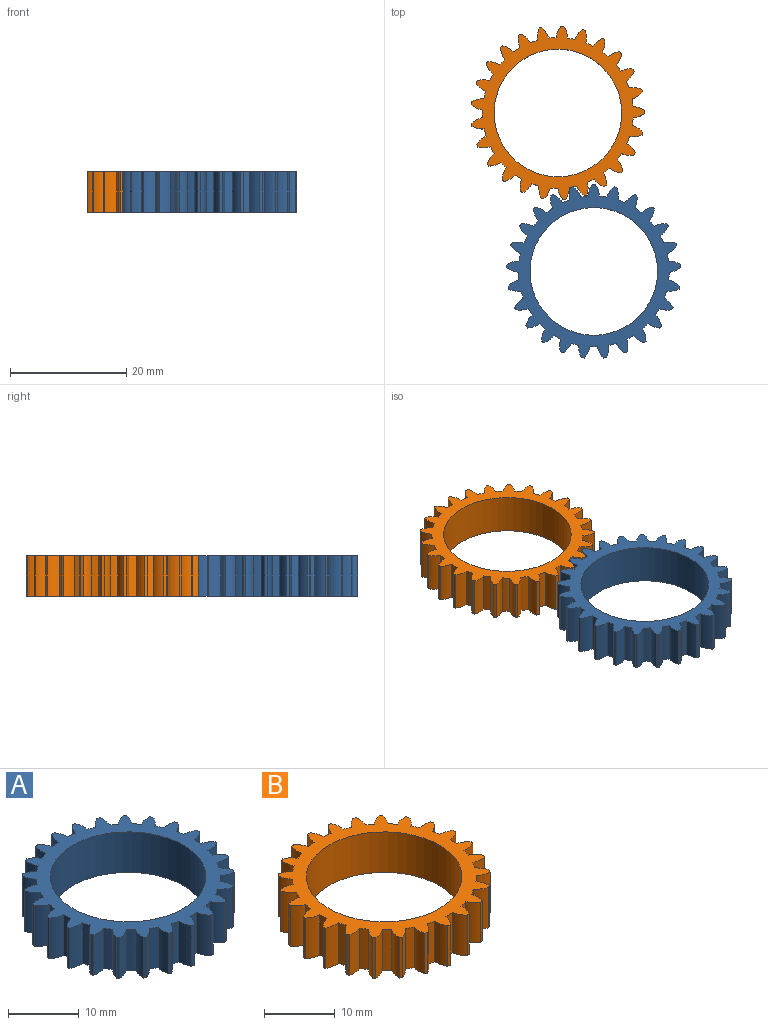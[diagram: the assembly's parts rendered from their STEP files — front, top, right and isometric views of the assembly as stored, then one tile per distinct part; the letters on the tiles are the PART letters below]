
ASSEMBLY  parts=2 mates=1
PART A: 103 faces, bbox 30x29.9x7 mm
  f0: cylinder r=4mm len=7mm, axis (0,0,-1), area 15.4mm2, adj f1,f3,f4,f32
  f1: cylinder r=15mm len=7mm, axis (0,0,-1), area 3.3mm2, adj f0,f2,f3,f4
  f2: cylinder r=4mm len=7mm, axis (0,0,-1), area 15.4mm2, adj f1,f3,f4,f5
  f3: plane 29.97x29.91mm, normal (0,0,1), area 222.8mm2, adj f0,f1,f2,f5,f6,f7,f8,f9
  f4: plane 29.97x29.91mm, normal (0,0,-1), area 222.8mm2, adj f0,f1,f2,f5,f6,f7,f8,f9
  f5: cylinder r=13mm len=7mm, axis (0,0,-1), area 9mm2, adj f2,f3,f4,f6
  f6: cylinder r=4mm len=7mm, axis (0,0,-1), area 15.4mm2, adj f3,f4,f5,f7
  f7: cylinder r=15mm len=7mm, axis (0,0,-1), area 3.3mm2, adj f3,f4,f6,f8
  f8: cylinder r=4mm len=7mm, axis (0,0,-1), area 15.4mm2, adj f3,f4,f7,f9
  f9: cylinder r=13mm len=7mm, axis (0,0,-1), area 9mm2, adj f3,f4,f8,f34
  f10: cylinder r=13mm len=7mm, axis (0,0,-1), area 9mm2, adj f3,f4,f99,f100
  f11: cylinder r=13mm len=7mm, axis (0,0,-1), area 9mm2, adj f3,f4,f96,f97
  f12: cylinder r=13mm len=7mm, axis (0,0,-1), area 9mm2, adj f3,f4,f93,f94
  f13: cylinder r=13mm len=7mm, axis (0,0,-1), area 9mm2, adj f3,f4,f90,f91
  f14: cylinder r=13mm len=7mm, axis (0,0,-1), area 9mm2, adj f3,f4,f87,f88
  f15: cylinder r=13mm len=7mm, axis (0,0,-1), area 9mm2, adj f3,f4,f84,f85
  f16: cylinder r=13mm len=7mm, axis (0,0,-1), area 9mm2, adj f3,f4,f81,f82
  f17: cylinder r=13mm len=7mm, axis (0,0,-1), area 9mm2, adj f3,f4,f78,f79
  f18: cylinder r=13mm len=7mm, axis (0,0,-1), area 9mm2, adj f3,f4,f75,f76
  f19: cylinder r=13mm len=7mm, axis (0,0,-1), area 9mm2, adj f3,f4,f72,f73
  f20: cylinder r=13mm len=7mm, axis (0,0,-1), area 9mm2, adj f3,f4,f69,f70
  f21: cylinder r=13mm len=7mm, axis (0,0,-1), area 9mm2, adj f3,f4,f66,f67
  f22: cylinder r=13mm len=7mm, axis (0,0,-1), area 9mm2, adj f3,f4,f63,f64
  f23: cylinder r=13mm len=7mm, axis (0,0,-1), area 9mm2, adj f3,f4,f60,f61
  f24: cylinder r=13mm len=7mm, axis (0,0,-1), area 9mm2, adj f3,f4,f57,f58
  f25: cylinder r=13mm len=7mm, axis (0,0,-1), area 9mm2, adj f3,f4,f54,f55
  f26: cylinder r=13mm len=7mm, axis (0,0,-1), area 9mm2, adj f3,f4,f51,f52
  f27: cylinder r=13mm len=7mm, axis (0,0,-1), area 9mm2, adj f3,f4,f48,f49
  f28: cylinder r=13mm len=7mm, axis (0,0,-1), area 9mm2, adj f3,f4,f45,f46
  f29: cylinder r=13mm len=7mm, axis (0,0,-1), area 9mm2, adj f3,f4,f42,f43
  f30: cylinder r=13mm len=7mm, axis (0,0,-1), area 9mm2, adj f3,f4,f39,f40
  f31: cylinder r=13mm len=7mm, axis (0,0,-1), area 9mm2, adj f3,f4,f36,f37
  f32: cylinder r=13mm len=7mm, axis (0,0,-1), area 9mm2, adj f0,f3,f4,f102
  f33: cylinder r=11mm len=22mm, axis (0,0,-1), area 483.8mm2, adj f3,f4
  f34: cylinder r=4mm len=7mm, axis (0,0,-1), area 15.4mm2, adj f3,f4,f9,f35
  f35: cylinder r=15mm len=7mm, axis (0,0,-1), area 3.3mm2, adj f3,f4,f34,f36
  f36: cylinder r=4mm len=7mm, axis (0,0,-1), area 15.4mm2, adj f3,f4,f31,f35
  f37: cylinder r=4mm len=7mm, axis (0,0,-1), area 15.4mm2, adj f3,f4,f31,f38
  f38: cylinder r=15mm len=7mm, axis (0,0,-1), area 3.3mm2, adj f3,f4,f37,f39
  f39: cylinder r=4mm len=7mm, axis (0,0,-1), area 15.4mm2, adj f3,f4,f30,f38
  f40: cylinder r=4mm len=7mm, axis (0,0,-1), area 15.4mm2, adj f3,f4,f30,f41
  f41: cylinder r=15mm len=7mm, axis (0,0,-1), area 3.3mm2, adj f3,f4,f40,f42
  f42: cylinder r=4mm len=7mm, axis (0,0,-1), area 15.4mm2, adj f3,f4,f29,f41
  f43: cylinder r=4mm len=7mm, axis (0,0,-1), area 15.4mm2, adj f3,f4,f29,f44
  f44: cylinder r=15mm len=7mm, axis (0,0,-1), area 3.3mm2, adj f3,f4,f43,f45
  f45: cylinder r=4mm len=7mm, axis (0,0,-1), area 15.4mm2, adj f3,f4,f28,f44
  f46: cylinder r=4mm len=7mm, axis (0,0,-1), area 15.4mm2, adj f3,f4,f28,f47
  f47: cylinder r=15mm len=7mm, axis (0,0,-1), area 3.3mm2, adj f3,f4,f46,f48
  f48: cylinder r=4mm len=7mm, axis (0,0,-1), area 15.4mm2, adj f3,f4,f27,f47
  f49: cylinder r=4mm len=7mm, axis (0,0,-1), area 15.4mm2, adj f3,f4,f27,f50
  f50: cylinder r=15mm len=7mm, axis (0,0,-1), area 3.3mm2, adj f3,f4,f49,f51
  f51: cylinder r=4mm len=7mm, axis (0,0,-1), area 15.4mm2, adj f3,f4,f26,f50
  f52: cylinder r=4mm len=7mm, axis (0,0,-1), area 15.4mm2, adj f3,f4,f26,f53
  f53: cylinder r=15mm len=7mm, axis (0,0,-1), area 3.3mm2, adj f3,f4,f52,f54
  f54: cylinder r=4mm len=7mm, axis (0,0,-1), area 15.4mm2, adj f3,f4,f25,f53
  f55: cylinder r=4mm len=7mm, axis (0,0,-1), area 15.4mm2, adj f3,f4,f25,f56
  f56: cylinder r=15mm len=7mm, axis (0,0,-1), area 3.3mm2, adj f3,f4,f55,f57
  f57: cylinder r=4mm len=7mm, axis (0,0,-1), area 15.4mm2, adj f3,f4,f24,f56
  f58: cylinder r=4mm len=7mm, axis (0,0,-1), area 15.4mm2, adj f3,f4,f24,f59
  f59: cylinder r=15mm len=7mm, axis (0,0,-1), area 3.3mm2, adj f3,f4,f58,f60
  f60: cylinder r=4mm len=7mm, axis (0,0,-1), area 15.4mm2, adj f3,f4,f23,f59
  f61: cylinder r=4mm len=7mm, axis (0,0,-1), area 15.4mm2, adj f3,f4,f23,f62
  f62: cylinder r=15mm len=7mm, axis (0,0,-1), area 3.3mm2, adj f3,f4,f61,f63
  f63: cylinder r=4mm len=7mm, axis (0,0,-1), area 15.4mm2, adj f3,f4,f22,f62
  f64: cylinder r=4mm len=7mm, axis (0,0,-1), area 15.4mm2, adj f3,f4,f22,f65
  f65: cylinder r=15mm len=7mm, axis (0,0,-1), area 3.3mm2, adj f3,f4,f64,f66
  f66: cylinder r=4mm len=7mm, axis (0,0,-1), area 15.4mm2, adj f3,f4,f21,f65
  f67: cylinder r=4mm len=7mm, axis (0,0,-1), area 15.4mm2, adj f3,f4,f21,f68
  f68: cylinder r=15mm len=7mm, axis (0,0,-1), area 3.3mm2, adj f3,f4,f67,f69
  f69: cylinder r=4mm len=7mm, axis (0,0,-1), area 15.4mm2, adj f3,f4,f20,f68
  f70: cylinder r=4mm len=7mm, axis (0,0,-1), area 15.4mm2, adj f3,f4,f20,f71
  f71: cylinder r=15mm len=7mm, axis (0,0,-1), area 3.3mm2, adj f3,f4,f70,f72
  f72: cylinder r=4mm len=7mm, axis (0,0,-1), area 15.4mm2, adj f3,f4,f19,f71
  f73: cylinder r=4mm len=7mm, axis (0,0,-1), area 15.4mm2, adj f3,f4,f19,f74
  f74: cylinder r=15mm len=7mm, axis (0,0,-1), area 3.3mm2, adj f3,f4,f73,f75
  f75: cylinder r=4mm len=7mm, axis (0,0,-1), area 15.4mm2, adj f3,f4,f18,f74
  f76: cylinder r=4mm len=7mm, axis (0,0,-1), area 15.4mm2, adj f3,f4,f18,f77
  f77: cylinder r=15mm len=7mm, axis (0,0,-1), area 3.3mm2, adj f3,f4,f76,f78
  f78: cylinder r=4mm len=7mm, axis (0,0,-1), area 15.4mm2, adj f3,f4,f17,f77
  f79: cylinder r=4mm len=7mm, axis (0,0,-1), area 15.4mm2, adj f3,f4,f17,f80
  f80: cylinder r=15mm len=7mm, axis (0,0,-1), area 3.3mm2, adj f3,f4,f79,f81
  f81: cylinder r=4mm len=7mm, axis (0,0,-1), area 15.4mm2, adj f3,f4,f16,f80
  f82: cylinder r=4mm len=7mm, axis (0,0,-1), area 15.4mm2, adj f3,f4,f16,f83
  f83: cylinder r=15mm len=7mm, axis (0,0,-1), area 3.3mm2, adj f3,f4,f82,f84
  f84: cylinder r=4mm len=7mm, axis (0,0,-1), area 15.4mm2, adj f3,f4,f15,f83
  f85: cylinder r=4mm len=7mm, axis (0,0,-1), area 15.4mm2, adj f3,f4,f15,f86
  f86: cylinder r=15mm len=7mm, axis (0,0,-1), area 3.3mm2, adj f3,f4,f85,f87
  f87: cylinder r=4mm len=7mm, axis (0,0,-1), area 15.4mm2, adj f3,f4,f14,f86
  f88: cylinder r=4mm len=7mm, axis (0,0,-1), area 15.4mm2, adj f3,f4,f14,f89
  f89: cylinder r=15mm len=7mm, axis (0,0,-1), area 3.3mm2, adj f3,f4,f88,f90
  f90: cylinder r=4mm len=7mm, axis (0,0,-1), area 15.4mm2, adj f3,f4,f13,f89
  f91: cylinder r=4mm len=7mm, axis (0,0,-1), area 15.4mm2, adj f3,f4,f13,f92
  f92: cylinder r=15mm len=7mm, axis (0,0,-1), area 3.3mm2, adj f3,f4,f91,f93
  f93: cylinder r=4mm len=7mm, axis (0,0,-1), area 15.4mm2, adj f3,f4,f12,f92
  f94: cylinder r=4mm len=7mm, axis (0,0,-1), area 15.4mm2, adj f3,f4,f12,f95
  f95: cylinder r=15mm len=7mm, axis (0,0,-1), area 3.3mm2, adj f3,f4,f94,f96
  f96: cylinder r=4mm len=7mm, axis (0,0,-1), area 15.4mm2, adj f3,f4,f11,f95
  f97: cylinder r=4mm len=7mm, axis (0,0,-1), area 15.4mm2, adj f3,f4,f11,f98
  f98: cylinder r=15mm len=7mm, axis (0,0,-1), area 3.3mm2, adj f3,f4,f97,f99
  f99: cylinder r=4mm len=7mm, axis (0,0,-1), area 15.4mm2, adj f3,f4,f10,f98
  f100: cylinder r=4mm len=7mm, axis (0,0,-1), area 15.4mm2, adj f3,f4,f10,f101
  f101: cylinder r=15mm len=7mm, axis (0,0,-1), area 3.3mm2, adj f3,f4,f100,f102
  f102: cylinder r=4mm len=7mm, axis (0,0,-1), area 15.4mm2, adj f3,f4,f32,f101
PART B: 103 faces, bbox 30x29.9x7 mm
  f0: cylinder r=4mm len=7mm, axis (0,0,-1), area 15.4mm2, adj f1,f3,f4,f32
  f1: cylinder r=15mm len=7mm, axis (0,0,-1), area 3.3mm2, adj f0,f2,f3,f4
  f2: cylinder r=4mm len=7mm, axis (0,0,-1), area 15.4mm2, adj f1,f3,f4,f5
  f3: plane 29.97x29.91mm, normal (0,0,1), area 222.8mm2, adj f0,f1,f2,f5,f6,f7,f8,f9
  f4: plane 29.97x29.91mm, normal (0,0,-1), area 222.8mm2, adj f0,f1,f2,f5,f6,f7,f8,f9
  f5: cylinder r=13mm len=7mm, axis (0,0,-1), area 9mm2, adj f2,f3,f4,f6
  f6: cylinder r=4mm len=7mm, axis (0,0,-1), area 15.4mm2, adj f3,f4,f5,f7
  f7: cylinder r=15mm len=7mm, axis (0,0,-1), area 3.3mm2, adj f3,f4,f6,f8
  f8: cylinder r=4mm len=7mm, axis (0,0,-1), area 15.4mm2, adj f3,f4,f7,f9
  f9: cylinder r=13mm len=7mm, axis (0,0,-1), area 9mm2, adj f3,f4,f8,f34
  f10: cylinder r=13mm len=7mm, axis (0,0,-1), area 9mm2, adj f3,f4,f99,f100
  f11: cylinder r=13mm len=7mm, axis (0,0,-1), area 9mm2, adj f3,f4,f96,f97
  f12: cylinder r=13mm len=7mm, axis (0,0,-1), area 9mm2, adj f3,f4,f93,f94
  f13: cylinder r=13mm len=7mm, axis (0,0,-1), area 9mm2, adj f3,f4,f90,f91
  f14: cylinder r=13mm len=7mm, axis (0,0,-1), area 9mm2, adj f3,f4,f87,f88
  f15: cylinder r=13mm len=7mm, axis (0,0,-1), area 9mm2, adj f3,f4,f84,f85
  f16: cylinder r=13mm len=7mm, axis (0,0,-1), area 9mm2, adj f3,f4,f81,f82
  f17: cylinder r=13mm len=7mm, axis (0,0,-1), area 9mm2, adj f3,f4,f78,f79
  f18: cylinder r=13mm len=7mm, axis (0,0,-1), area 9mm2, adj f3,f4,f75,f76
  f19: cylinder r=13mm len=7mm, axis (0,0,-1), area 9mm2, adj f3,f4,f72,f73
  f20: cylinder r=13mm len=7mm, axis (0,0,-1), area 9mm2, adj f3,f4,f69,f70
  f21: cylinder r=13mm len=7mm, axis (0,0,-1), area 9mm2, adj f3,f4,f66,f67
  f22: cylinder r=13mm len=7mm, axis (0,0,-1), area 9mm2, adj f3,f4,f63,f64
  f23: cylinder r=13mm len=7mm, axis (0,0,-1), area 9mm2, adj f3,f4,f60,f61
  f24: cylinder r=13mm len=7mm, axis (0,0,-1), area 9mm2, adj f3,f4,f57,f58
  f25: cylinder r=13mm len=7mm, axis (0,0,-1), area 9mm2, adj f3,f4,f54,f55
  f26: cylinder r=13mm len=7mm, axis (0,0,-1), area 9mm2, adj f3,f4,f51,f52
  f27: cylinder r=13mm len=7mm, axis (0,0,-1), area 9mm2, adj f3,f4,f48,f49
  f28: cylinder r=13mm len=7mm, axis (0,0,-1), area 9mm2, adj f3,f4,f45,f46
  f29: cylinder r=13mm len=7mm, axis (0,0,-1), area 9mm2, adj f3,f4,f42,f43
  f30: cylinder r=13mm len=7mm, axis (0,0,-1), area 9mm2, adj f3,f4,f39,f40
  f31: cylinder r=13mm len=7mm, axis (0,0,-1), area 9mm2, adj f3,f4,f36,f37
  f32: cylinder r=13mm len=7mm, axis (0,0,-1), area 9mm2, adj f0,f3,f4,f102
  f33: cylinder r=11mm len=22mm, axis (0,0,-1), area 483.8mm2, adj f3,f4
  f34: cylinder r=4mm len=7mm, axis (0,0,-1), area 15.4mm2, adj f3,f4,f9,f35
  f35: cylinder r=15mm len=7mm, axis (0,0,-1), area 3.3mm2, adj f3,f4,f34,f36
  f36: cylinder r=4mm len=7mm, axis (0,0,-1), area 15.4mm2, adj f3,f4,f31,f35
  f37: cylinder r=4mm len=7mm, axis (0,0,-1), area 15.4mm2, adj f3,f4,f31,f38
  f38: cylinder r=15mm len=7mm, axis (0,0,-1), area 3.3mm2, adj f3,f4,f37,f39
  f39: cylinder r=4mm len=7mm, axis (0,0,-1), area 15.4mm2, adj f3,f4,f30,f38
  f40: cylinder r=4mm len=7mm, axis (0,0,-1), area 15.4mm2, adj f3,f4,f30,f41
  f41: cylinder r=15mm len=7mm, axis (0,0,-1), area 3.3mm2, adj f3,f4,f40,f42
  f42: cylinder r=4mm len=7mm, axis (0,0,-1), area 15.4mm2, adj f3,f4,f29,f41
  f43: cylinder r=4mm len=7mm, axis (0,0,-1), area 15.4mm2, adj f3,f4,f29,f44
  f44: cylinder r=15mm len=7mm, axis (0,0,-1), area 3.3mm2, adj f3,f4,f43,f45
  f45: cylinder r=4mm len=7mm, axis (0,0,-1), area 15.4mm2, adj f3,f4,f28,f44
  f46: cylinder r=4mm len=7mm, axis (0,0,-1), area 15.4mm2, adj f3,f4,f28,f47
  f47: cylinder r=15mm len=7mm, axis (0,0,-1), area 3.3mm2, adj f3,f4,f46,f48
  f48: cylinder r=4mm len=7mm, axis (0,0,-1), area 15.4mm2, adj f3,f4,f27,f47
  f49: cylinder r=4mm len=7mm, axis (0,0,-1), area 15.4mm2, adj f3,f4,f27,f50
  f50: cylinder r=15mm len=7mm, axis (0,0,-1), area 3.3mm2, adj f3,f4,f49,f51
  f51: cylinder r=4mm len=7mm, axis (0,0,-1), area 15.4mm2, adj f3,f4,f26,f50
  f52: cylinder r=4mm len=7mm, axis (0,0,-1), area 15.4mm2, adj f3,f4,f26,f53
  f53: cylinder r=15mm len=7mm, axis (0,0,-1), area 3.3mm2, adj f3,f4,f52,f54
  f54: cylinder r=4mm len=7mm, axis (0,0,-1), area 15.4mm2, adj f3,f4,f25,f53
  f55: cylinder r=4mm len=7mm, axis (0,0,-1), area 15.4mm2, adj f3,f4,f25,f56
  f56: cylinder r=15mm len=7mm, axis (0,0,-1), area 3.3mm2, adj f3,f4,f55,f57
  f57: cylinder r=4mm len=7mm, axis (0,0,-1), area 15.4mm2, adj f3,f4,f24,f56
  f58: cylinder r=4mm len=7mm, axis (0,0,-1), area 15.4mm2, adj f3,f4,f24,f59
  f59: cylinder r=15mm len=7mm, axis (0,0,-1), area 3.3mm2, adj f3,f4,f58,f60
  f60: cylinder r=4mm len=7mm, axis (0,0,-1), area 15.4mm2, adj f3,f4,f23,f59
  f61: cylinder r=4mm len=7mm, axis (0,0,-1), area 15.4mm2, adj f3,f4,f23,f62
  f62: cylinder r=15mm len=7mm, axis (0,0,-1), area 3.3mm2, adj f3,f4,f61,f63
  f63: cylinder r=4mm len=7mm, axis (0,0,-1), area 15.4mm2, adj f3,f4,f22,f62
  f64: cylinder r=4mm len=7mm, axis (0,0,-1), area 15.4mm2, adj f3,f4,f22,f65
  f65: cylinder r=15mm len=7mm, axis (0,0,-1), area 3.3mm2, adj f3,f4,f64,f66
  f66: cylinder r=4mm len=7mm, axis (0,0,-1), area 15.4mm2, adj f3,f4,f21,f65
  f67: cylinder r=4mm len=7mm, axis (0,0,-1), area 15.4mm2, adj f3,f4,f21,f68
  f68: cylinder r=15mm len=7mm, axis (0,0,-1), area 3.3mm2, adj f3,f4,f67,f69
  f69: cylinder r=4mm len=7mm, axis (0,0,-1), area 15.4mm2, adj f3,f4,f20,f68
  f70: cylinder r=4mm len=7mm, axis (0,0,-1), area 15.4mm2, adj f3,f4,f20,f71
  f71: cylinder r=15mm len=7mm, axis (0,0,-1), area 3.3mm2, adj f3,f4,f70,f72
  f72: cylinder r=4mm len=7mm, axis (0,0,-1), area 15.4mm2, adj f3,f4,f19,f71
  f73: cylinder r=4mm len=7mm, axis (0,0,-1), area 15.4mm2, adj f3,f4,f19,f74
  f74: cylinder r=15mm len=7mm, axis (0,0,-1), area 3.3mm2, adj f3,f4,f73,f75
  f75: cylinder r=4mm len=7mm, axis (0,0,-1), area 15.4mm2, adj f3,f4,f18,f74
  f76: cylinder r=4mm len=7mm, axis (0,0,-1), area 15.4mm2, adj f3,f4,f18,f77
  f77: cylinder r=15mm len=7mm, axis (0,0,-1), area 3.3mm2, adj f3,f4,f76,f78
  f78: cylinder r=4mm len=7mm, axis (0,0,-1), area 15.4mm2, adj f3,f4,f17,f77
  f79: cylinder r=4mm len=7mm, axis (0,0,-1), area 15.4mm2, adj f3,f4,f17,f80
  f80: cylinder r=15mm len=7mm, axis (0,0,-1), area 3.3mm2, adj f3,f4,f79,f81
  f81: cylinder r=4mm len=7mm, axis (0,0,-1), area 15.4mm2, adj f3,f4,f16,f80
  f82: cylinder r=4mm len=7mm, axis (0,0,-1), area 15.4mm2, adj f3,f4,f16,f83
  f83: cylinder r=15mm len=7mm, axis (0,0,-1), area 3.3mm2, adj f3,f4,f82,f84
  f84: cylinder r=4mm len=7mm, axis (0,0,-1), area 15.4mm2, adj f3,f4,f15,f83
  f85: cylinder r=4mm len=7mm, axis (0,0,-1), area 15.4mm2, adj f3,f4,f15,f86
  f86: cylinder r=15mm len=7mm, axis (0,0,-1), area 3.3mm2, adj f3,f4,f85,f87
  f87: cylinder r=4mm len=7mm, axis (0,0,-1), area 15.4mm2, adj f3,f4,f14,f86
  f88: cylinder r=4mm len=7mm, axis (0,0,-1), area 15.4mm2, adj f3,f4,f14,f89
  f89: cylinder r=15mm len=7mm, axis (0,0,-1), area 3.3mm2, adj f3,f4,f88,f90
  f90: cylinder r=4mm len=7mm, axis (0,0,-1), area 15.4mm2, adj f3,f4,f13,f89
  f91: cylinder r=4mm len=7mm, axis (0,0,-1), area 15.4mm2, adj f3,f4,f13,f92
  f92: cylinder r=15mm len=7mm, axis (0,0,-1), area 3.3mm2, adj f3,f4,f91,f93
  f93: cylinder r=4mm len=7mm, axis (0,0,-1), area 15.4mm2, adj f3,f4,f12,f92
  f94: cylinder r=4mm len=7mm, axis (0,0,-1), area 15.4mm2, adj f3,f4,f12,f95
  f95: cylinder r=15mm len=7mm, axis (0,0,-1), area 3.3mm2, adj f3,f4,f94,f96
  f96: cylinder r=4mm len=7mm, axis (0,0,-1), area 15.4mm2, adj f3,f4,f11,f95
  f97: cylinder r=4mm len=7mm, axis (0,0,-1), area 15.4mm2, adj f3,f4,f11,f98
  f98: cylinder r=15mm len=7mm, axis (0,0,-1), area 3.3mm2, adj f3,f4,f97,f99
  f99: cylinder r=4mm len=7mm, axis (0,0,-1), area 15.4mm2, adj f3,f4,f10,f98
  f100: cylinder r=4mm len=7mm, axis (0,0,-1), area 15.4mm2, adj f3,f4,f10,f101
  f101: cylinder r=15mm len=7mm, axis (0,0,-1), area 3.3mm2, adj f3,f4,f100,f102
  f102: cylinder r=4mm len=7mm, axis (0,0,-1), area 15.4mm2, adj f3,f4,f32,f101
PLACE A t=(-3.76,1.17,4.91)mm fixed
PLACE B rot(axis=(0,0,1),11.4deg) t=(-4.37,0.93,4.91)mm
MATE revolute B.f3 <-> A.f1  axis (0,0,1) through (-3.76,1.17,11.91)mm
